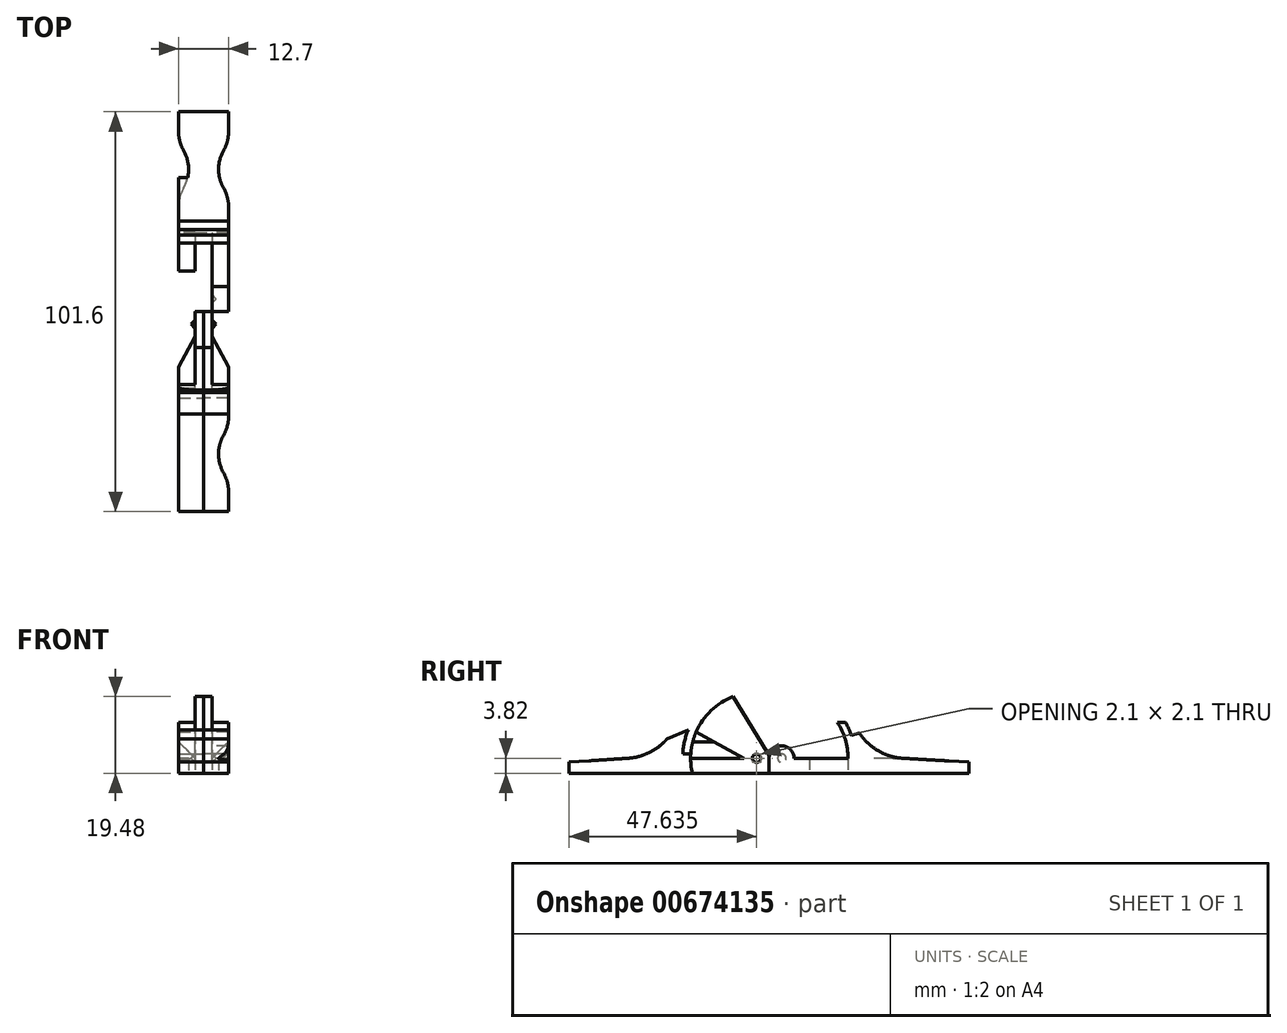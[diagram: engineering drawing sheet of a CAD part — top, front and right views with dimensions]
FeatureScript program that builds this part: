
annotation { "Feature Type Name" : "Feature", "Feature Type Description" : "" }
export const myFeature = defineFeature(function(context is Context, id is Id, definition is map)
    precondition{}
    {
        {
            var Q0;
            Q0=qCreatedBy(makeId("Right.planeOp"),FACE);
            var sketch = newSketch(context, id + "F0", { "sketchPlane" : qUnion([Q0])});
            skLineSegment(sketch, "E0", {"start": v(0, 0) * mm, "end": v(50.8, 0) * mm});
            skLineSegment(sketch, "E1", {"start": v(50.8, 0) * mm, "end": v(50.8, 2.83) * mm});
            skLineSegment(sketch, "E2", {"start": v(50.8, 2.83) * mm, "end": v(34.04, 3.8) * mm});
            skLineSegment(sketch, "E3", {"start": v(6.35, 3.8) * mm, "end": v(20.05, 3.8) * mm});
            skLineSegment(sketch, "E4", {"start": v(17.37, 12.94) * mm, "end": v(19.4, 12.94) * mm});
            skLineSegment(sketch, "E5", {"start": v(20.88, 9.58) * mm, "end": v(22.99, 10.2) * mm});
            skArc(sketch, "E6", {"start": v(34.04, 3.8) * mm, "mid": v(27.76, 5.7) * mm, "end": v(22.99, 10.2) * mm});
            skCircle(sketch, "E7", {"center": v(3.18, 3.8) * mm, "radius": 3.18 * mm});
            skLineSegment(sketch, "E8", {"start": v(0, 0) * mm, "end": v(0, 3.8) * mm});
            skArc(sketch, "E9", {"start": v(20.05, 3.8) * mm, "mid": v(19.37, 8.57) * mm, "end": v(17.37, 12.94) * mm});
            skArc(sketch, "E10", {"start": v(20.88, 9.58) * mm, "mid": v(20.23, 11.3) * mm, "end": v(19.4, 12.94) * mm});
            skSolve(sketch);
        }
        {
            var Q0;
            Q0 = qSketchRegion(id + "F0", true);
            extrude(context, id + "F1", {"entities" : qUnion([Q0]), "endBound" : BoundingType.SYMMETRIC, "depth" : 12.7 * mm, "offsetDistance" : 25.4 * mm});
        }
        {
            var Q0;
            Q0=qCreatedBy(makeId("Top.planeOp"),FACE);
            var sketch = newSketch(context, id + "F2", { "sketchPlane" : qUnion([Q0])});
            skLineSegment(sketch, "E11", {"start": v(0, 20.05) * mm, "end": v(2.12, 20.05) * mm});
            skLineSegment(sketch, "E12", {"start": v(2.12, 20.05) * mm, "end": v(2.12, 0) * mm});
            skLineSegment(sketch, "E13", {"start": v(2.12, 0) * mm, "end": v(0, 0) * mm});
            skLineSegment(sketch, "E14", {"start": v(4.23, 0) * mm, "end": v(6.35, 0) * mm, "construction": true});
            skPoint(sketch, "E15", {"position": v(4.23, 0) * mm});
            skLineSegment(sketch, "E16", {"start": v(2.12, 0) * mm, "end": v(4.23, 0) * mm, "construction": true});
            skArc(sketch, "E17", {"start": v(5.08, 40.96) * mm, "mid": v(6.03, 43.26) * mm, "end": v(6.35, 45.72) * mm});
            skArc(sketch, "E18", {"start": v(5.08, 40.96) * mm, "mid": v(3.81, 36.2) * mm, "end": v(5.08, 31.43) * mm});
            skArc(sketch, "E19", {"start": v(6.35, 26.67) * mm, "mid": v(6.03, 29.13) * mm, "end": v(5.08, 31.43) * mm});
            skLineSegment(sketch, "E20", {"start": v(6.35, 45.72) * mm, "end": v(6.35, 26.67) * mm});
            skLineSegment(sketch, "E21.MirrorCS", {"start": v(-2.12, 0) * mm, "end": v(-4.23, 0) * mm, "construction": true});
            skLineSegment(sketch, "E22.MirrorCS", {"start": v(-2.12, 0) * mm, "end": v(0, 0) * mm});
            skLineSegment(sketch, "E23.MirrorCS", {"start": v(-4.23, 0) * mm, "end": v(-6.35, 0) * mm, "construction": true});
            skArc(sketch, "E24.MirrorCS", {"start": v(-5.08, 40.96) * mm, "mid": v(-6.03, 43.26) * mm, "end": v(-6.35, 45.72) * mm});
            skArc(sketch, "E25.MirrorCS", {"start": v(-6.35, 26.67) * mm, "mid": v(-6.03, 29.13) * mm, "end": v(-5.08, 31.43) * mm});
            skLineSegment(sketch, "E26.MirrorCS", {"start": v(0, 20.05) * mm, "end": v(-2.12, 20.05) * mm});
            skArc(sketch, "E27.MirrorCS", {"start": v(-5.08, 40.96) * mm, "mid": v(-3.81, 36.2) * mm, "end": v(-5.08, 31.43) * mm});
            skLineSegment(sketch, "E28.MirrorCS", {"start": v(-6.35, 45.72) * mm, "end": v(-6.35, 26.67) * mm});
            skLineSegment(sketch, "E29.MirrorCS", {"start": v(-2.12, 20.05) * mm, "end": v(-2.12, 0) * mm});
            skPoint(sketch, "E30.MirrorP", {"position": v(-4.23, 0) * mm});
            skLineSegment(sketch, "E31", {"start": v(-2.12, 6.35) * mm, "end": v(2.12, 6.35) * mm});
            skSolve(sketch);
        }
        {
            var Q0;
            Q0 = qSketchRegion(id + "F2", true);
            var Q1;
            Q1=makeQuery(id+"F1.opExtrude","SWEPT_FACE",FACE,{"disambiguationData":[OSD([sQuery(id+"F0.wireOp",EDGE,"E3")])]});
            extrude(context, id + "F3", {"entities" : qUnion([Q0]), "operationType" : NewBodyOperationType.REMOVE, "endBound" : BoundingType.UP_TO_SURFACE, "depth" : 25.4 * mm, "endBoundEntityFace" : qUnion([Q1]), "offsetDistance" : 25.4 * mm});
        }
        {
            var Q0;
            Q0=makeQuery(id+"F2.imprint","IMPRINT",FACE,{"disambiguationData":[TD([[makeQuery(id+"F2.imprint","IMPRINT",EDGE,{"derivedFrom":sQuery(id+"F2.wireOp",EDGE,"E17")}),-1.0]])]});
            var Q1;
            Q1=makeQuery(id+"F2.imprint","IMPRINT",FACE,{"disambiguationData":[TD([[makeQuery(id+"F2.imprint","IMPRINT",EDGE,{"derivedFrom":sQuery(id+"F2.wireOp",EDGE,"E24.MirrorCS")}),1.0]])]});
            var Q2;
            {var subQ3=sQuery(id+"F2.wireOp",EDGE,"E13");Q2=makeQuery(id+"F2.imprint","IMPRINT",FACE,{"disambiguationData":[TD([[makeQuery(id+"F2.imprint","IMPRINT",EDGE,{"derivedFrom":subQ3}),-1.0]])]});}
            extrude(context, id + "F4", {"entities" : qUnion([Q0, Q1, Q2]), "operationType" : NewBodyOperationType.REMOVE, "depth" : 25.4 * mm, "offsetDistance" : 25.4 * mm});
        }
        {
            var Q0;
            Q0=qCreatedBy(makeId("Right.planeOp"),FACE);
            var sketch = newSketch(context, id + "F5", { "sketchPlane" : qUnion([Q0])});
            skLineSegment(sketch, "E32", {"start": v(0, 0) * mm, "end": v(0, 3.81) * mm});
            skLineSegment(sketch, "E33", {"start": v(0, 0) * mm, "end": v(-50.8, 0) * mm});
            skLineSegment(sketch, "E34", {"start": v(-50.8, 0) * mm, "end": v(-50.8, 2.83) * mm});
            skLineSegment(sketch, "E35", {"start": v(-50.8, 2.83) * mm, "end": v(-35.8, 3.81) * mm});
            skCircle(sketch, "E36", {"center": v(-3.18, 3.8) * mm, "radius": 3.18 * mm});
            skLineSegment(sketch, "E37", {"start": v(-6.35, 3.8) * mm, "end": v(-9.11, 19.48) * mm});
            skArc(sketch, "E38", {"start": v(-9.11, 19.48) * mm, "mid": v(-16.63, 13.8) * mm, "end": v(-19.89, 4.95) * mm});
            skArc(sketch, "E39", {"start": v(-20.5, 11.06) * mm, "mid": v(-21.47, 8.07) * mm, "end": v(-21.93, 4.95) * mm});
            skLineSegment(sketch, "E40", {"start": v(-19.89, 4.95) * mm, "end": v(-21.93, 4.95) * mm});
            skLineSegment(sketch, "E41", {"start": v(-20.5, 11.06) * mm, "end": v(-26, 8.68) * mm});
            skArc(sketch, "E42", {"start": v(-35.8, 3.81) * mm, "mid": v(-30.41, 5.26) * mm, "end": v(-26, 8.68) * mm});
            skArc(sketch, "E43", {"start": v(-19.89, 4.95) * mm, "mid": v(-19.92, 4.38) * mm, "end": v(-19.93, 3.8) * mm, "construction": true});
            skLineSegment(sketch, "E44", {"start": v(-19.93, 3.8) * mm, "end": v(-6.35, 3.8) * mm, "construction": true});
            skLineSegment(sketch, "E45", {"start": v(-9.11, 19.48) * mm, "end": v(-0.47, 5.48) * mm});
            skSolve(sketch);
        }
        {
            var Q0;
            Q0 = qSketchRegion(id + "F5", true);
            extrude(context, id + "F6", {"entities" : qUnion([Q0]), "endBound" : BoundingType.SYMMETRIC, "depth" : 12.7 * mm, "offsetDistance" : 25.4 * mm});
        }
        {
            var Q0;
            Q0=makeQuery(id+"F6.opExtrude","CAP_FACE",FACE,{"disambiguationData":[OSD([sQuery(id+"F5.wireOp",EDGE,"E32"),sQuery(id+"F5.wireOp",EDGE,"E33"),sQuery(id+"F5.wireOp",EDGE,"E34"),sQuery(id+"F5.wireOp",EDGE,"E35"),sQuery(id+"F5.wireOp",EDGE,"E36"),sQuery(id+"F5.wireOp",EDGE,"E37"),sQuery(id+"F5.wireOp",EDGE,"E38"),sQuery(id+"F5.wireOp",EDGE,"E39"),sQuery(id+"F5.wireOp",EDGE,"E40"),sQuery(id+"F5.wireOp",EDGE,"E41"),sQuery(id+"F5.wireOp",EDGE,"E42")])],"isStart":false});
            var sketch = newSketch(context, id + "F7", { "sketchPlane" : qUnion([Q0])});
            skCircle(sketch, "E46", {"center": v(-3.18, 3.8) * mm, "radius": 3.18 * mm});
            skLineSegment(sketch, "E47.bottom", {"start": v(0, 3.8) * mm, "end": v(0, 3.8) * mm});
            skLineSegment(sketch, "E47.top", {"start": v(0, 0) * mm, "end": v(0, 0) * mm});
            skLineSegment(sketch, "E47.left", {"start": v(0, 3.81) * mm, "end": v(0, 0) * mm});
            skLineSegment(sketch, "E47.right", {"start": v(0, 3.8) * mm, "end": v(0, 0) * mm});
            skLineSegment(sketch, "E48", {"start": v(0, 0) * mm, "end": v(-19.49, 0) * mm});
            skArc(sketch, "E49", {"start": v(-19.89, 4.95) * mm, "mid": v(-19.87, 2.46) * mm, "end": v(-19.49, 0) * mm});
            skArc(sketch, "E50", {"start": v(-9.11, 19.48) * mm, "mid": v(-16.63, 13.8) * mm, "end": v(-19.89, 4.95) * mm});
            skLineSegment(sketch, "E51", {"start": v(-9.11, 19.48) * mm, "end": v(-0.47, 5.48) * mm});
            skSolve(sketch);
        }
        {
            var Q0;
            Q0=qCreatedBy(makeId("Right.planeOp"),FACE);
            var sketch = newSketch(context, id + "F8", { "sketchPlane" : qUnion([Q0])});
            skCircle(sketch, "E52", {"center": v(3.24, 3.8) * mm, "radius": 1.27 * mm});
            skSolve(sketch);
        }
        {
            var Q0;
            Q0=makeQuery(id+"F8.imprint","IMPRINT",FACE,{"disambiguationData":[TD([[makeQuery(id+"F8.imprint","IMPRINT",EDGE,{"derivedFrom":sQuery(id+"F8.wireOp",EDGE,"E52")}),1.0]])]});
            extrude(context, id + "F9", {"entities" : qUnion([Q0]), "operationType" : NewBodyOperationType.REMOVE, "endBound" : BoundingType.SYMMETRIC, "depth" : 6.35 * mm, "offsetDistance" : 25.4 * mm});
        }
        {
            var Q0;
            Q0=makeQuery(id+"F9.boolean.opBoolean","COPY",EDGE,{"derivedFrom":makeQuery(id+"F9.opExtrude","CAP_EDGE",EDGE,{"disambiguationData":[OSD([sQuery(id+"F8.wireOp",EDGE,"E52")])],"isStart":true})});
            var Q1;
            Q1=makeQuery(id+"F9.boolean.opBoolean","COPY",EDGE,{"derivedFrom":makeQuery(id+"F9.opExtrude","CAP_EDGE",EDGE,{"disambiguationData":[OSD([sQuery(id+"F8.wireOp",EDGE,"E52")])],"isStart":false})});
            chamfer(context, id + "F10", {"entities" : qUnion([Q0, Q1]), "width" : 1.27 * mm, "tangentPropagation" : true});
        }
        {
            var Q0;
            Q0 = qSketchRegion(id + "F7", true);
            var Q1;
            Q1=makeQuery(id+"F7.imprint","IMPRINT",FACE,{"disambiguationData":[TD([[makeQuery(id+"F7.imprint","IMPRINT",EDGE,{"derivedFrom":sQuery(id+"F7.wireOp",EDGE,"E47.left")}),-1.0]])]});
            var Q2;
            {var subQ0=sQuery(id+"F2.wireOp",EDGE,"E12");Q2=makeQuery(id+"F4.boolean.opBoolean","MERGE",FACE,{"derivedFrom":[makeQuery(id+"F3.boolean.opBoolean","COPY",FACE,{"derivedFrom":makeQuery(id+"F3.opExtrude","SWEPT_FACE",FACE,{"disambiguationData":[OSD([subQ0])]})})],"fromTools":[makeQuery(id+"F4.opExtrude","SWEPT_FACE",FACE,{"disambiguationData":[OSD([subQ0])]})]});}
            extrude(context, id + "F11", {"entities" : qUnion([Q0, Q1]), "operationType" : NewBodyOperationType.REMOVE, "endBound" : BoundingType.UP_TO_SURFACE, "oppositeDirection" : true, "depth" : 25.4 * mm, "endBoundEntityFace" : qUnion([Q2]), "offsetDistance" : 25.4 * mm});
        }
        {
            var Q0;
            Q0=qCreatedBy(makeId("Right.planeOp"),FACE);
            var sketch = newSketch(context, id + "F12", { "sketchPlane" : qUnion([Q0])});
            skCircle(sketch, "E53", {"center": v(-3.18, 3.8) * mm, "radius": 1.27 * mm});
            skSolve(sketch);
        }
        {
            var Q0;
            Q0 = qSketchRegion(id + "F12", true);
            extrude(context, id + "F13", {"entities" : qUnion([Q0]), "operationType" : NewBodyOperationType.ADD, "endBound" : BoundingType.SYMMETRIC, "depth" : 6.35 * mm, "offsetDistance" : 25.4 * mm});
        }
        {
            var Q0;
            Q0=makeQuery(id+"F13.opExtrude","CAP_EDGE",EDGE,{"disambiguationData":[OSD([sQuery(id+"F12.wireOp",EDGE,"E53")])],"isStart":false});
            chamfer(context, id + "F14", {"entities" : qUnion([Q0]), "width" : 1.27 * mm, "tangentPropagation" : true});
        }
        {
            var Q0;
            Q0=makeQuery(id+"F11.boolean.opBoolean","COPY",FACE,{"derivedFrom":makeQuery(id+"F11.opExtrude","CAP_FACE",FACE,{"disambiguationData":[OSD([sQuery(id+"F7.wireOp",EDGE,"E46"),sQuery(id+"F7.wireOp",EDGE,"E47.right"),sQuery(id+"F7.wireOp",EDGE,"E48"),sQuery(id+"F7.wireOp",EDGE,"E49"),sQuery(id+"F7.wireOp",EDGE,"E50"),sQuery(id+"F7.wireOp",EDGE,"E51")])],"isStart":false})});
            var sketch = newSketch(context, id + "F15", { "sketchPlane" : qUnion([Q0])});
            skLineSegment(sketch, "E54", {"start": v(-18.53, 10.51) * mm, "end": v(-6.35, 3.8) * mm});
            skLineSegment(sketch, "E55", {"start": v(-6.35, 3.8) * mm, "end": v(-19.93, 3.8) * mm});
            skArc(sketch, "E56", {"start": v(-18.53, 10.51) * mm, "mid": v(-19.57, 7.23) * mm, "end": v(-19.93, 3.8) * mm});
            skCircle(sketch, "E57", {"center": v(-3.17, 3.8) * mm, "radius": 3.17 * mm, "construction": true});
            skSolve(sketch);
        }
        {
            var Q0;
            Q0=makeQuery(id+"F15.imprint","IMPRINT",FACE,{"disambiguationData":[TD([[makeQuery(id+"F15.imprint","IMPRINT",EDGE,{"derivedFrom":sQuery(id+"F15.wireOp",EDGE,"E54")}),-1.0]])]});
            var Q1;
            Q1=makeQuery(id+"F6.opExtrude","CAP_FACE",FACE,{"disambiguationData":[OSD([sQuery(id+"F5.wireOp",EDGE,"E32"),sQuery(id+"F5.wireOp",EDGE,"E33"),sQuery(id+"F5.wireOp",EDGE,"E34"),sQuery(id+"F5.wireOp",EDGE,"E35"),sQuery(id+"F5.wireOp",EDGE,"E36"),sQuery(id+"F5.wireOp",EDGE,"E37"),sQuery(id+"F5.wireOp",EDGE,"E38"),sQuery(id+"F5.wireOp",EDGE,"E39"),sQuery(id+"F5.wireOp",EDGE,"E40"),sQuery(id+"F5.wireOp",EDGE,"E41"),sQuery(id+"F5.wireOp",EDGE,"E42")])],"isStart":false});
            extrude(context, id + "F16", {"entities" : qUnion([Q0]), "operationType" : NewBodyOperationType.ADD, "endBound" : BoundingType.UP_TO_SURFACE, "depth" : 25.4 * mm, "endBoundEntityFace" : qUnion([Q1]), "offsetDistance" : 25.4 * mm});
        }
        {
            var Q0;
            Q0=makeQuery(id+"F16.opExtrude","CAP_EDGE",EDGE,{"disambiguationData":[OSD([sQuery(id+"F15.wireOp",EDGE,"E55")])],"isStart":false});
            chamfer(context, id + "F17", {"entities" : qUnion([Q0]), "width" : 4.22 * mm, "tangentPropagation" : true});
        }
        {
            var Q0;
            Q0=qCreatedBy(makeId("Right.planeOp"),FACE);
            var sketch = newSketch(context, id + "F18", { "sketchPlane" : qUnion([Q0])});
            skLineSegment(sketch, "E58.bottom", {"start": v(10.26, 31.85) * mm, "end": v(-66.33, 31.85) * mm});
            skLineSegment(sketch, "E58.top", {"start": v(10.26, -12.9) * mm, "end": v(-66.33, -12.9) * mm});
            skLineSegment(sketch, "E58.left", {"start": v(10.26, 31.85) * mm, "end": v(10.26, -12.9) * mm});
            skLineSegment(sketch, "E58.right", {"start": v(-66.33, 31.85) * mm, "end": v(-66.33, -12.9) * mm});
            skSolve(sketch);
        }
        {
            var Q0;
            Q0=makeQuery(id+"F18.imprint","IMPRINT",FACE,{"disambiguationData":[TD([[makeQuery(id+"F18.imprint","IMPRINT",EDGE,{"derivedFrom":sQuery(id+"F18.wireOp",EDGE,"E58.bottom")}),1.0]])]});
            extrude(context, id + "F19", {"entities" : qUnion([Q0]), "operationType" : NewBodyOperationType.REMOVE, "oppositeDirection" : true, "depth" : 25.4 * mm, "offsetDistance" : 25.4 * mm});
        }
        {
            var Q0;
            Q0=makeQuery(id+"F6.opExtrude","SWEPT_BODY",BODY,{"disambiguationData":[OSD([sQuery(id+"F5.wireOp",EDGE,"E32"),sQuery(id+"F5.wireOp",EDGE,"E33"),sQuery(id+"F5.wireOp",EDGE,"E34"),sQuery(id+"F5.wireOp",EDGE,"E35"),sQuery(id+"F5.wireOp",EDGE,"E36"),sQuery(id+"F5.wireOp",EDGE,"E38"),sQuery(id+"F5.wireOp",EDGE,"E39"),sQuery(id+"F5.wireOp",EDGE,"E40"),sQuery(id+"F5.wireOp",EDGE,"E41"),sQuery(id+"F5.wireOp",EDGE,"E42"),sQuery(id+"F5.wireOp",EDGE,"E45")])]});
            var Q1;
            Q1=qCreatedBy(makeId("Right.planeOp"),FACE);
            mirror(context, id + "F20", {"operationType" : NewBodyOperationType.ADD, "entities" : qUnion([Q0]), "mirrorPlane" : qUnion([Q1])});
        }
        {
            var Q0;
            Q0=qCreatedBy(makeId("Top.planeOp"),FACE);
            var sketch = newSketch(context, id + "F21", { "sketchPlane" : qUnion([Q0])});
            skArc(sketch, "E59", {"start": v(6.35, -45.72) * mm, "mid": v(6.03, -43.26) * mm, "end": v(5.08, -40.96) * mm});
            skArc(sketch, "E60", {"start": v(5.08, -31.43) * mm, "mid": v(3.8, -36.2) * mm, "end": v(5.08, -40.96) * mm});
            skArc(sketch, "E61", {"start": v(5.08, -31.43) * mm, "mid": v(6.03, -29.13) * mm, "end": v(6.35, -26.67) * mm});
            skPoint(sketch, "E62", {"position": v(3.81, -36.2) * mm});
            skPoint(sketch, "E63.MirrorP", {"position": v(-3.81, -36.2) * mm});
            skArc(sketch, "E64.MirrorCS", {"start": v(-5.08, -31.43) * mm, "mid": v(-3.8, -36.2) * mm, "end": v(-5.08, -40.96) * mm});
            skArc(sketch, "E65.MirrorCS", {"start": v(-5.08, -31.43) * mm, "mid": v(-6.03, -29.13) * mm, "end": v(-6.35, -26.67) * mm});
            skArc(sketch, "E66.MirrorCS", {"start": v(-6.35, -45.72) * mm, "mid": v(-6.03, -43.26) * mm, "end": v(-5.08, -40.96) * mm});
            skLineSegment(sketch, "E67", {"start": v(6.35, -26.67) * mm, "end": v(6.35, -45.72) * mm});
            skLineSegment(sketch, "E68", {"start": v(-6.35, -26.67) * mm, "end": v(-6.35, -45.72) * mm});
            skSolve(sketch);
        }
        {
            var Q0;
            Q0=makeQuery(id+"F21.imprint","IMPRINT",FACE,{"disambiguationData":[TD([[makeQuery(id+"F21.imprint","IMPRINT",EDGE,{"derivedFrom":sQuery(id+"F21.wireOp",EDGE,"E64.MirrorCS")}),-1.0]])]});
            var Q1;
            Q1=makeQuery(id+"F21.imprint","IMPRINT",FACE,{"disambiguationData":[TD([[makeQuery(id+"F21.imprint","IMPRINT",EDGE,{"derivedFrom":sQuery(id+"F21.wireOp",EDGE,"E59")}),-1.0]])]});
            extrude(context, id + "F22", {"entities" : qUnion([Q0, Q1]), "operationType" : NewBodyOperationType.REMOVE, "depth" : 25.4 * mm, "offsetDistance" : 25.4 * mm});
        }
    });
